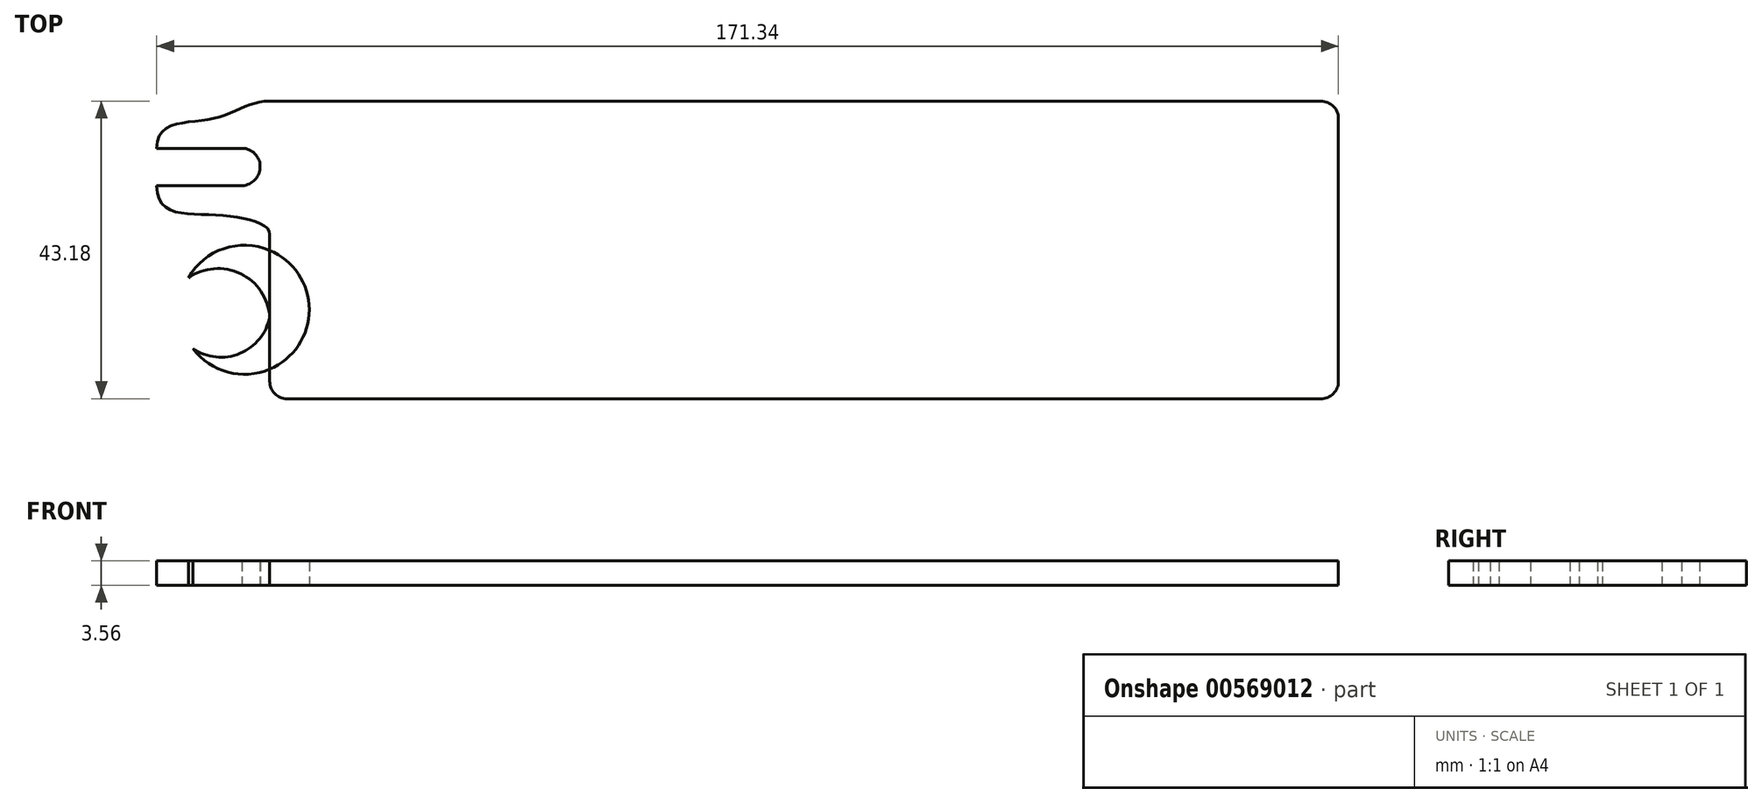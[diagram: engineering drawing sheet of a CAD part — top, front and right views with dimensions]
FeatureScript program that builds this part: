
annotation { "Feature Type Name" : "Feature", "Feature Type Description" : "" }
export const myFeature = defineFeature(function(context is Context, id is Id, definition is map)
    precondition{}
    {
        {
            var Q0;
            Q0=qCreatedBy(makeId("Top.planeOp"),FACE);
            var sketch = newSketch(context, id + "F0", { "sketchPlane" : qUnion([Q0])});
            skLineSegment(sketch, "E0.bottom", {"start": v(-88.4, 31.3) * mm, "end": v(64, 31.3) * mm});
            skLineSegment(sketch, "E0.top", {"start": v(-85.85, -11.88) * mm, "end": v(64, -11.88) * mm});
            skLineSegment(sketch, "E0.left", {"start": v(-88.4, 31.3) * mm, "end": v(-88.4, -9.34) * mm});
            skLineSegment(sketch, "E0.right", {"start": v(66.55, 28.76) * mm, "end": v(66.55, -9.34) * mm});
            skFitSpline(sketch, "E1", {"points": [v(-88.4, 31.3) * mm, v(-96.87, 28.7) * mm, v(-104.8, 24.45) * mm], "startDerivative": vector(-17.98, 0.55) * mm, "endDerivative": vector(0, -25.41) * mm});
            skLineSegment(sketch, "E2", {"start": v(-104.8, 24.45) * mm, "end": v(-92.38, 24.45) * mm});
            skArc(sketch, "E3", {"start": v(-89.78, 21.86) * mm, "mid": v(-90.55, 23.7) * mm, "end": v(-92.38, 24.45) * mm});
            skArc(sketch, "E4", {"start": v(-92.38, 19.03) * mm, "mid": v(-90.51, 19.92) * mm, "end": v(-89.78, 21.86) * mm});
            skLineSegment(sketch, "E5", {"start": v(-92.38, 19.03) * mm, "end": v(-104.8, 19.03) * mm});
            skFitSpline(sketch, "E6", {"points": [v(-104.8, 19.03) * mm, v(-96.47, 14.8) * mm, v(-88.4, 12.01) * mm], "startDerivative": vector(0.38, -26.74) * mm, "endDerivative": vector(0, -10.52) * mm});
            skCircle(sketch, "E7", {"center": v(-92.03, 1.04) * mm, "radius": 9.37 * mm});
            skPoint(sketch, "E8.visualSharp", {"position": v(66.55, 31.3) * mm});
            skArc(sketch, "E8.filletArc", {"start": v(66.55, 28.76) * mm, "mid": v(65.8, 30.56) * mm, "end": v(64, 31.3) * mm});
            skPoint(sketch, "E9.visualSharp", {"position": v(66.55, -11.88) * mm});
            skArc(sketch, "E9.filletArc", {"start": v(64, -11.88) * mm, "mid": v(65.8, -11.14) * mm, "end": v(66.55, -9.34) * mm});
            skPoint(sketch, "E10.visualSharp", {"position": v(-88.4, -11.88) * mm});
            skArc(sketch, "E10.filletArc", {"start": v(-88.4, -9.34) * mm, "mid": v(-87.65, -11.14) * mm, "end": v(-85.85, -11.88) * mm});
            skArc(sketch, "E11", {"start": v(-88.4, 0) * mm, "mid": v(-92.63, 6.28) * mm, "end": v(-100.18, 5.66) * mm});
            skArc(sketch, "E12", {"start": v(-99.5, -4.62) * mm, "mid": v(-92.7, -5.3) * mm, "end": v(-88.4, 0) * mm});
            skLineSegment(sketch, "E13.bottom", {"start": v(-76.96, 25.59) * mm, "end": v(-35, 25.59) * mm});
            skLineSegment(sketch, "E13.top", {"start": v(-76.96, -4.23) * mm, "end": v(-35, -4.23) * mm});
            skLineSegment(sketch, "E13.left", {"start": v(-76.96, 25.59) * mm, "end": v(-76.96, -4.23) * mm});
            skLineSegment(sketch, "E13.right", {"start": v(-35, 25.59) * mm, "end": v(-35, -4.23) * mm});
            skSolve(sketch);
        }
        {
            var Q0;
            {var subQ0=sQuery(id+"F0.wireOp",EDGE,"E1");Q0=makeQuery(id+"F0.imprint","IMPRINT",FACE,{"disambiguationData":[TD([[makeQuery(id+"F0.imprint","IMPRINT",EDGE,{"derivedFrom":subQ0}),1.0]])]});}
            var Q1;
            {var subQ0=sQuery(id+"F0.wireOp",EDGE,"E11");Q1=makeQuery(id+"F0.imprint","IMPRINT",FACE,{"disambiguationData":[TD([[makeQuery(id+"F0.imprint","IMPRINT",EDGE,{"derivedFrom":subQ0}),-1.0]])]});}
            var Q2;
            {var subQ0=sQuery(id+"F0.wireOp",EDGE,"E12");Q2=makeQuery(id+"F0.imprint","IMPRINT",FACE,{"disambiguationData":[TD([[makeQuery(id+"F0.imprint","IMPRINT",EDGE,{"derivedFrom":subQ0}),-1.0]])]});}
            var Q3;
            {var subQ5=sQuery(id+"F0.wireOp",EDGE,"E0.bottom");Q3=makeQuery(id+"F0.imprint","IMPRINT",FACE,{"disambiguationData":[TD([[makeQuery(id+"F0.imprint","IMPRINT",EDGE,{"derivedFrom":subQ5}),-1.0]])]});}
            var Q4;
            Q4=makeQuery(id+"F0.imprint","IMPRINT",FACE,{"disambiguationData":[TD([[makeQuery(id+"F0.imprint","IMPRINT",EDGE,{"derivedFrom":sQuery(id+"F0.wireOp",EDGE,"E13.bottom")}),-1.0]])]});
            extrude(context, id + "F1", {"entities" : qUnion([Q0, Q1, Q2, Q3, Q4]), "depth" : 3.56 * mm, "offsetDistance" : 25.4 * mm});
        }
    });
